# Revit family: Plumbing-P_Trap-Waterworks-Universal-Bottle
name_source: partatom
category: Pipe Fittings
revit_build: Autodesk Revit MEP 2014 (Build: 20140709_2115(x64)
units: mm (PartAtom-declared; Revit-internal decimal feet)

## types (18) — shared parameters
ADA Compliant = No
Assembly Code = D2030100
Certification IAPMO = Yes
Certification cUPC = Yes
Code Compliance = Code # FDMS48: IAPMO
Default Elevation = 2' - 10"
Height = 0' - 6"
Inlet Connection Diameter = 0' - 1 1/4"
Inlet Connection Type = Compression
Keynote = 22 40 00
Length = 0' - 3 3/8"
Manufacturer = Waterworks
Model = UNPT48
Outlet Connection Diameter = 0' - 1 1/4"
Outlet Connection Type = Compression
Product Documentation Link = http://assets.waterworks.com
Product Page URL = http://www.waterworks.com
URL = http://www.waterworks.com
Version = 2014 - v1.0a
Warranty = http://www.waterworks.com

## per-type parameters (varying)
| type | Constraint | Description | Finish | Long Trim | Model SKU | Product Name | Short Trim |
| Antique Brass | 1 | Universal Bottle P-Trap 1 1/4” x 1 1/4” in Antique Brass | Metal - Waterworks - Antique Brass | No | 26-57556-90087 | Universal Bottle P-Trap 1 1/4” x 1 1/4” in Antique Brass | Yes |
| Antique Copper | 2 | Universal Bottle P-Trap 1 1/4” x 1 1/4” in Antique Copper | Metal - Waterworks - Antique Copper | Yes | 26-62587-94842 | Universal Bottle P-Trap 1 1/4” x 1 1/4” in Antique Copper | No |
| Architectural Bronze | 3 | Universal Bottle P-Trap 1 1/4” x 1 1/4” in Architectural Bronze | Metal - Waterworks - Architectural Bronze | Yes | 26-40631-12688 | Universal Bottle P-Trap 1 1/4” x 1 1/4” in Architectural Bronze | No |
| Burnished Brass | 4 | Universal Bottle P-Trap 1 1/4” x 1 1/4” in Burnished Brass | Metal - Waterworks - Burnished Brass | Yes | 26-94599-61223 | Universal Bottle P-Trap 1 1/4” x 1 1/4” in Burnished Brass | No |
| Burnished Nickel | 5 | Universal Bottle P-Trap 1 1/4” x 1 1/4” in Burnished Nickel | Metal - Waterworks - Burnished Nickel | Yes | 26-63763-00089 | Universal Bottle P-Trap 1 1/4” x 1 1/4” in Burnished Nickel | No |
| Carbon | 6 | Universal Bottle P-Trap 1 1/4” x 1 1/4” in Carbon | Metal - Waterworks - Carbon | Yes | 26-82948-70959 | Universal Bottle P-Trap 1 1/4” x 1 1/4” in Carbon | No |
| Chrome | 7 | Universal Bottle P-Trap 1 1/4” x 1 1/4” in Chrome | Metal - Waterworks - Chrome | Yes | 26-18724-89858 | Universal Bottle P-Trap 1 1/4” x 1 1/4” in Chrome | No |
| Gold | 9 | Universal Bottle P-Trap 1 1/4” x 1 1/4” in Gold | Metal - Waterworks - Gold | Yes | 26-62730-05487 | Universal Bottle P-Trap 1 1/4” x 1 1/4” in Gold | No |
| Graphite | 10 | Universal Bottle P-Trap 1 1/4” x 1 1/4” in Graphite | Metal - Waterworks - Graphite | Yes | 26-98710-34046 | Universal Bottle P-Trap 1 1/4” x 1 1/4” in Graphite | No |
| Matte Gold | 12 | Universal Bottle P-Trap 1 1/4” x 1 1/4” in Matte Gold | Metal - Waterworks - Matte Gold | Yes | 26-91861-35228 | Universal Bottle P-Trap 1 1/4” x 1 1/4” in Matte Gold | No |
| Matte Nickel | 13 | Universal Bottle P-Trap 1 1/4” x 1 1/4” in Matte Nickel | Metal - Waterworks - Matte Nickel | Yes | 26-72110-64618 | Universal Bottle P-Trap 1 1/4” x 1 1/4” in Matte Nickel | No |
| Nickel | 15 | Universal Bottle P-Trap 1 1/4” x 1 1/4” in Nickel | Metal - Waterworks - Nickel | Yes | 26-42850-56092 | Universal Bottle P-Trap 1 1/4” x 1 1/4” in Nickel | No |
| Pewter | 16 | Universal Bottle P-Trap 1 1/4” x 1 1/4” in Pewter | Metal - Waterworks - Pewter | Yes | 26-46710-93284 | Universal Bottle P-Trap 1 1/4” x 1 1/4” in Pewter | No |
| Polished Brass | 17 | Universal Bottle P-Trap 1 1/4” x 1 1/4” in Polished Brass | Metal - Waterworks - Polished Brass | Yes | 26-77908-31775 | Universal Bottle P-Trap 1 1/4” x 1 1/4” in Polished Brass | No |
| Shiny Copper | 18 | Universal Bottle P-Trap 1 1/4” x 1 1/4” in Shiny Copper | Metal - Waterworks - Shiny Copper | Yes | 26-84191-70435 | Universal Bottle P-Trap 1 1/4” x 1 1/4” in Shiny Copper | No |
| Sovereign | 20 | Universal Bottle P-Trap 1 1/4” x 1 1/4” in Sovereign | Metal - Waterworks - Sovereign | Yes | 26-55055-94707 | Universal Bottle P-Trap 1 1/4” x 1 1/4” in Sovereign | No |
| Unlacquered Brass | 21 | Universal Bottle P-Trap 1 1/4” x 1 1/4” in Unlacquered Brass | Metal - Waterworks - Unlacquered Brass | Yes | 26-98829-12014 | Universal Bottle P-Trap 1 1/4” x 1 1/4” in Unlacquered Brass | No |
| Vintage Brass | 22 | Universal Bottle P-Trap 1 1/4” x 1 1/4” in Vintage Brass | Metal - Waterworks - Vintage Brass | Yes | 26-34163-64881 | Universal Bottle P-Trap 1 1/4” x 1 1/4” in Vintage Brass | No |

## geometry (parser evidence)
native form markers: Sweep x6
no freeform markers — native parametric forms only
